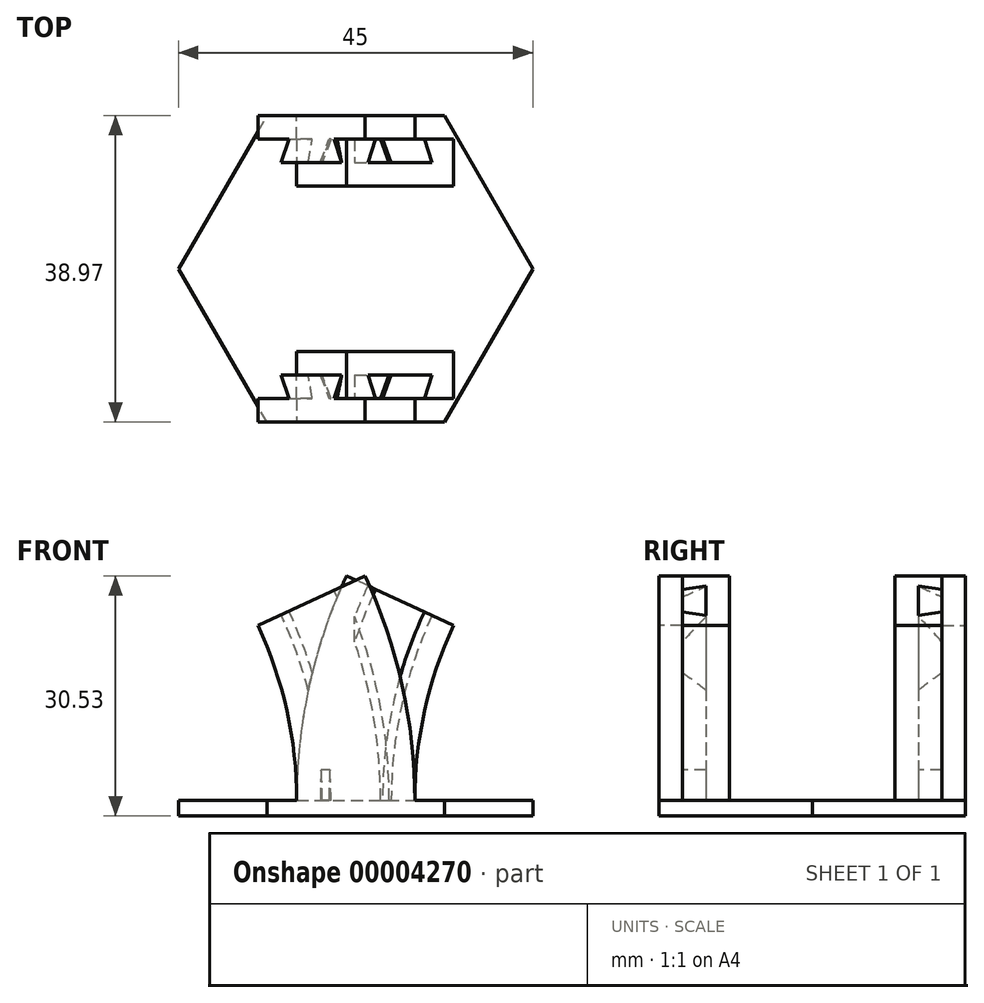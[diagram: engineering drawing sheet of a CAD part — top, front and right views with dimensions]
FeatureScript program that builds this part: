
annotation { "Feature Type Name" : "Feature", "Feature Type Description" : "" }
export const myFeature = defineFeature(function(context is Context, id is Id, definition is map)
    precondition{}
    {
        {
            var Q0;
            Q0=qCreatedBy(makeId("Top.planeOp"),FACE);
            var sketch = newSketch(context, id + "F0", { "sketchPlane" : qUnion([Q0])});
            skPoint(sketch, "E0", {"position": v(0, 0) * mm});
            skLineSegment(sketch, "E1", {"start": v(-7.5, 0) * mm, "end": v(7.5, 0) * mm});
            skLineSegment(sketch, "E2", {"start": v(7.5, 0) * mm, "end": v(7.5, 6) * mm});
            skLineSegment(sketch, "E3", {"start": v(7.5, 6) * mm, "end": v(3.4, 6) * mm});
            skLineSegment(sketch, "E4", {"start": v(3.4, 6) * mm, "end": v(4.5, 3) * mm});
            skLineSegment(sketch, "E5", {"start": v(4.5, 3) * mm, "end": v(-4.5, 3) * mm});
            skLineSegment(sketch, "E6", {"start": v(-4.5, 3) * mm, "end": v(-3.4, 6) * mm});
            skLineSegment(sketch, "E7", {"start": v(-3.4, 6) * mm, "end": v(-7.5, 6) * mm});
            skLineSegment(sketch, "E8", {"start": v(-7.5, 6) * mm, "end": v(-7.5, 3) * mm});
            skPoint(sketch, "E9", {"position": v(-7.5, 3) * mm});
            skLineSegment(sketch, "E10", {"start": v(-7.5, 3) * mm, "end": v(-4.5, 3) * mm, "construction": true});
            skLineSegment(sketch, "E11", {"start": v(-7.5, 3) * mm, "end": v(-7.5, 0) * mm});
            skLineSegment(sketch, "E12", {"start": v(-7.5, 6) * mm, "end": v(-7.5, 9) * mm});
            skLineSegment(sketch, "E13", {"start": v(-7.5, 9) * mm, "end": v(7.5, 9) * mm});
            skLineSegment(sketch, "E14", {"start": v(7.5, 9) * mm, "end": v(7.5, 6) * mm});
            skCircle(sketch, "E15.cCircle", {"center": v(0, -10.49) * mm, "radius": 22.5 * mm, "construction": true});
            skLineSegment(sketch, "E15.0", {"start": v(11.25, -29.97) * mm, "end": v(-11.25, -29.97) * mm});
            skLineSegment(sketch, "E15.1", {"start": v(-11.25, -29.97) * mm, "end": v(-22.5, -10.49) * mm});
            skLineSegment(sketch, "E15.2", {"start": v(-22.5, -10.49) * mm, "end": v(-11.25, 9) * mm});
            skLineSegment(sketch, "E15.3", {"start": v(-11.25, 9) * mm, "end": v(11.25, 9) * mm});
            skLineSegment(sketch, "E15.4", {"start": v(11.25, 9) * mm, "end": v(22.5, -10.49) * mm});
            skLineSegment(sketch, "E15.5", {"start": v(22.5, -10.49) * mm, "end": v(11.25, -29.97) * mm});
            skLineSegment(sketch, "E16", {"start": v(-3.16, 6) * mm, "end": v(-4.25, 3) * mm});
            skLineSegment(sketch, "E17", {"start": v(3.16, 6) * mm, "end": v(4.25, 3) * mm});
            skLineSegment(sketch, "E18", {"start": v(-3.4, 6) * mm, "end": v(-3.16, 6) * mm});
            skLineSegment(sketch, "E19", {"start": v(3.16, 6) * mm, "end": v(3.4, 6) * mm});
            skLineSegment(sketch, "E20", {"start": v(-60, -10.49) * mm, "end": v(60, -10.49) * mm, "construction": true});
            skLineSegment(sketch, "E21.0.MirrorCS", {"start": v(-7.5, -20.97) * mm, "end": v(7.5, -20.97) * mm});
            skLineSegment(sketch, "E22.0.MirrorCS", {"start": v(-7.5, -23.97) * mm, "end": v(-7.5, -20.97) * mm});
            skLineSegment(sketch, "E23.0.MirrorCS", {"start": v(-7.5, -26.97) * mm, "end": v(-7.5, -23.97) * mm});
            skLineSegment(sketch, "E24.0.MirrorCS", {"start": v(-3.4, -26.97) * mm, "end": v(-7.5, -26.97) * mm});
            skLineSegment(sketch, "E25.0.MirrorCS", {"start": v(-7.5, -26.97) * mm, "end": v(-7.5, -29.97) * mm});
            skLineSegment(sketch, "E26.0.MirrorCS", {"start": v(-7.5, -29.97) * mm, "end": v(7.5, -29.97) * mm});
            skLineSegment(sketch, "E27.0.MirrorCS", {"start": v(-4.5, -23.97) * mm, "end": v(-3.4, -26.97) * mm});
            skLineSegment(sketch, "E28.0.MirrorCS", {"start": v(-3.16, -26.97) * mm, "end": v(-4.25, -23.97) * mm});
            skLineSegment(sketch, "E29.0.MirrorCS", {"start": v(4.5, -23.97) * mm, "end": v(-4.5, -23.97) * mm});
            skLineSegment(sketch, "E30.0.MirrorCS", {"start": v(3.16, -26.97) * mm, "end": v(4.25, -23.97) * mm});
            skLineSegment(sketch, "E31.0.MirrorCS", {"start": v(3.4, -26.97) * mm, "end": v(4.5, -23.97) * mm});
            skLineSegment(sketch, "E32.0.MirrorCS", {"start": v(7.5, -26.97) * mm, "end": v(3.4, -26.97) * mm});
            skLineSegment(sketch, "E33.0.MirrorCS", {"start": v(7.5, -20.97) * mm, "end": v(7.5, -26.97) * mm});
            skLineSegment(sketch, "E34.0.MirrorCS", {"start": v(7.5, -29.97) * mm, "end": v(7.5, -26.97) * mm});
            skLineSegment(sketch, "E35", {"start": v(-60, 9) * mm, "end": v(-60, -29.97) * mm, "construction": true});
            skLineSegment(sketch, "E36.0.MirrorCS", {"start": v(-3.4, -26.97) * mm, "end": v(-3.16, -26.97) * mm});
            skLineSegment(sketch, "E37.0.MirrorCS", {"start": v(3.16, -26.97) * mm, "end": v(3.4, -26.97) * mm});
            skLineSegment(sketch, "E38", {"start": v(60, -29.97) * mm, "end": v(60, 9) * mm, "construction": true});
            skSolve(sketch);
        }
        {
            var Q0;
            Q0=makeQuery(id+"F0.imprint","IMPRINT",FACE,{"disambiguationData":[TD([[makeQuery(id+"F0.imprint","IMPRINT",EDGE,{"derivedFrom":sQuery(id+"F0.wireOp",EDGE,"E1")}),-1.0]])]});
            var Q1;
            Q1=makeQuery(id+"F0.imprint","IMPRINT",FACE,{"disambiguationData":[TD([[makeQuery(id+"F0.imprint","IMPRINT",EDGE,{"derivedFrom":sQuery(id+"F0.wireOp",EDGE,"E22.0.MirrorCS")}),-1.0]])]});
            var Q2;
            Q2=makeQuery(id+"F0.imprint","IMPRINT",FACE,{"disambiguationData":[TD([[makeQuery(id+"F0.imprint","IMPRINT",EDGE,{"derivedFrom":sQuery(id+"F0.wireOp",EDGE,"E24.0.MirrorCS")}),1.0]])]});
            var Q3;
            Q3=makeQuery(id+"F0.imprint","IMPRINT",FACE,{"disambiguationData":[TD([[makeQuery(id+"F0.imprint","IMPRINT",EDGE,{"derivedFrom":sQuery(id+"F0.wireOp",EDGE,"E1")}),1.0]])]});
            var Q4;
            {var subQ1=sQuery(id+"F0.wireOp",EDGE,"E6");Q4=makeQuery(id+"F0.imprint","IMPRINT",FACE,{"disambiguationData":[TD([[makeQuery(id+"F0.imprint","IMPRINT",EDGE,{"derivedFrom":subQ1}),-1.0]])]});}
            var Q5;
            Q5=makeQuery(id+"F0.imprint","IMPRINT",FACE,{"disambiguationData":[TD([[makeQuery(id+"F0.imprint","IMPRINT",EDGE,{"derivedFrom":sQuery(id+"F0.wireOp",EDGE,"E3")}),-1.0]])]});
            var Q6;
            {var subQ2=sQuery(id+"F0.wireOp",EDGE,"E4");Q6=makeQuery(id+"F0.imprint","IMPRINT",FACE,{"disambiguationData":[TD([[makeQuery(id+"F0.imprint","IMPRINT",EDGE,{"derivedFrom":subQ2}),-1.0]])]});}
            extrude(context, id + "F1", {"entities" : qUnion([Q0, Q1, Q2, Q3, Q4, Q5, Q6]), "oppositeDirection" : true, "depth" : 2 * mm});
        }
        {
            var Q0;
            Q0=makeQuery(id+"F0.imprint","IMPRINT",FACE,{"disambiguationData":[TD([[makeQuery(id+"F0.imprint","IMPRINT",EDGE,{"derivedFrom":sQuery(id+"F0.wireOp",EDGE,"E3")}),-1.0]])]});
            var Q1;
            Q1=makeQuery(id+"F0.imprint","IMPRINT",FACE,{"disambiguationData":[TD([[makeQuery(id+"F0.imprint","IMPRINT",EDGE,{"derivedFrom":sQuery(id+"F0.wireOp",EDGE,"E24.0.MirrorCS")}),1.0]])]});
            var Q2;
            Q2=sQuery(id+"F0.wireOp",EDGE,"E35");
            revolve(context, id + "F2", {"operationType" : NewBodyOperationType.ADD, "entities" : qUnion([Q0, Q1]), "axis" : qUnion([Q2]), "revolveType" : RevolveType.ONE_DIRECTION, "angle" : 25 * degree});
        }
        {
            var Q0;
            Q0=makeQuery(id+"F0.imprint","IMPRINT",FACE,{"disambiguationData":[TD([[makeQuery(id+"F0.imprint","IMPRINT",EDGE,{"derivedFrom":sQuery(id+"F0.wireOp",EDGE,"E1")}),-1.0]])]});
            var Q1;
            Q1=makeQuery(id+"F0.imprint","IMPRINT",FACE,{"disambiguationData":[TD([[makeQuery(id+"F0.imprint","IMPRINT",EDGE,{"derivedFrom":sQuery(id+"F0.wireOp",EDGE,"E22.0.MirrorCS")}),-1.0]])]});
            var Q2;
            Q2=makeQuery(id+"F0.imprint","IMPRINT",FACE,{"disambiguationData":[TD([[makeQuery(id+"F0.imprint","IMPRINT",EDGE,{"derivedFrom":sQuery(id+"F0.wireOp",EDGE,"E24.0.MirrorCS")}),1.0]])]});
            var Q3;
            {var subQ2=sQuery(id+"F0.wireOp",EDGE,"E30.0.MirrorCS");Q3=makeQuery(id+"F0.imprint","IMPRINT",FACE,{"disambiguationData":[TD([[makeQuery(id+"F0.imprint","IMPRINT",EDGE,{"derivedFrom":subQ2}),-1.0]])]});}
            var Q4;
            {var subQ2=sQuery(id+"F0.wireOp",EDGE,"E27.0.MirrorCS");Q4=makeQuery(id+"F0.imprint","IMPRINT",FACE,{"disambiguationData":[TD([[makeQuery(id+"F0.imprint","IMPRINT",EDGE,{"derivedFrom":subQ2}),1.0]])]});}
            var Q5;
            {var subQ2=sQuery(id+"F0.wireOp",EDGE,"E4");Q5=makeQuery(id+"F0.imprint","IMPRINT",FACE,{"disambiguationData":[TD([[makeQuery(id+"F0.imprint","IMPRINT",EDGE,{"derivedFrom":subQ2}),-1.0]])]});}
            var Q6;
            Q6=makeQuery(id+"F0.imprint","IMPRINT",FACE,{"disambiguationData":[TD([[makeQuery(id+"F0.imprint","IMPRINT",EDGE,{"derivedFrom":sQuery(id+"F0.wireOp",EDGE,"E1")}),1.0]])]});
            var Q7;
            Q7=makeQuery(id+"F0.imprint","IMPRINT",FACE,{"disambiguationData":[TD([[makeQuery(id+"F0.imprint","IMPRINT",EDGE,{"derivedFrom":sQuery(id+"F0.wireOp",EDGE,"E3")}),-1.0]])]});
            var Q8;
            {var subQ1=sQuery(id+"F0.wireOp",EDGE,"E6");Q8=makeQuery(id+"F0.imprint","IMPRINT",FACE,{"disambiguationData":[TD([[makeQuery(id+"F0.imprint","IMPRINT",EDGE,{"derivedFrom":subQ1}),-1.0]])]});}
            extrude(context, id + "F3", {"entities" : qUnion([Q0, Q1, Q2, Q3, Q4, Q5, Q6, Q7, Q8]), "oppositeDirection" : true, "depth" : 2 * mm});
        }
        {
            var Q0;
            Q0=makeQuery(id+"F0.imprint","IMPRINT",FACE,{"disambiguationData":[TD([[makeQuery(id+"F0.imprint","IMPRINT",EDGE,{"derivedFrom":sQuery(id+"F0.wireOp",EDGE,"E1")}),1.0]])]});
            var Q1;
            Q1=makeQuery(id+"F0.imprint","IMPRINT",FACE,{"disambiguationData":[TD([[makeQuery(id+"F0.imprint","IMPRINT",EDGE,{"derivedFrom":sQuery(id+"F0.wireOp",EDGE,"E22.0.MirrorCS")}),-1.0]])]});
            var Q2;
            Q2=sQuery(id+"F0.wireOp",EDGE,"E38");
            revolve(context, id + "F4", {"operationType" : NewBodyOperationType.ADD, "entities" : qUnion([Q0, Q1]), "axis" : qUnion([Q2]), "revolveType" : RevolveType.ONE_DIRECTION, "angle" : 25 * degree});
        }
    });
